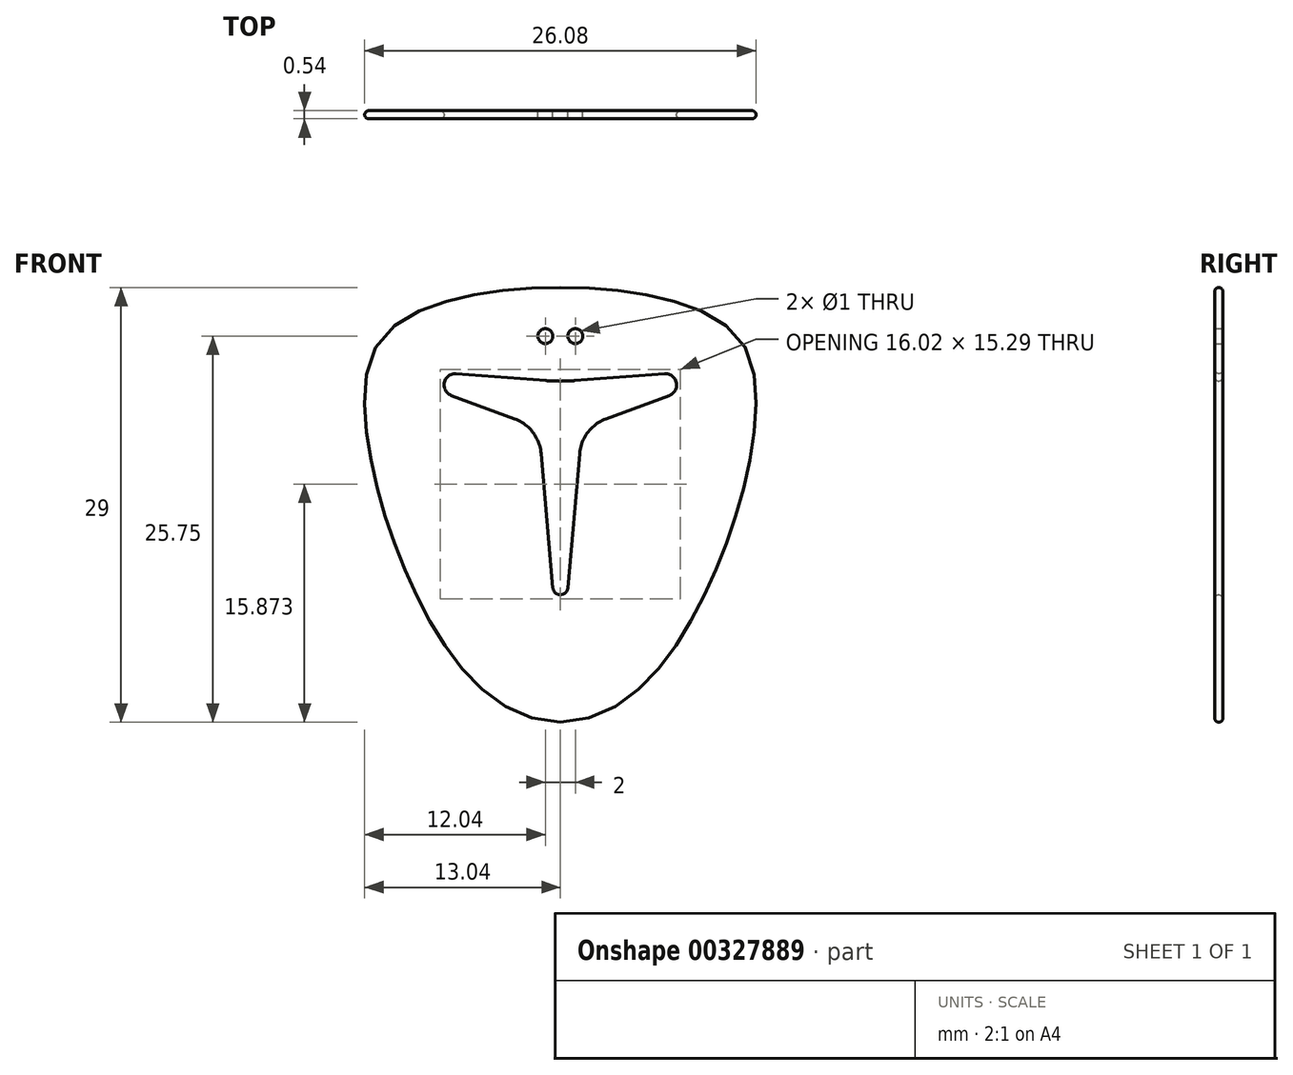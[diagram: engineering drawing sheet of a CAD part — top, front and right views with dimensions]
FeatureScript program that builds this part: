
annotation { "Feature Type Name" : "Feature", "Feature Type Description" : "" }
export const myFeature = defineFeature(function(context is Context, id is Id, definition is map)
    precondition{}
    {
        {
            var Q0;
            Q0=qCreatedBy(makeId("Front.planeOp"),FACE);
            var sketch = newSketch(context, id + "F0", { "sketchPlane" : qUnion([Q0])});
            skLineSegment(sketch, "E0", {"start": v(0, 0) * mm, "end": v(0, 6.5) * mm, "construction": true});
            skLineSegment(sketch, "E1", {"start": v(0, 0) * mm, "end": v(0, -22.5) * mm, "construction": true});
            skLineSegment(sketch, "E2", {"start": v(0, 0) * mm, "end": v(13, 0) * mm, "construction": true});
            skFitSpline(sketch, "E3", {"points": [v(0, -22.5) * mm, v(10.5, -12) * mm, v(13, 0) * mm, v(11, 4) * mm, v(0, 6.5) * mm], "startDerivative": vector(49.93, 0) * mm, "endDerivative": vector(-57.3, 0) * mm});
            skFitSpline(sketch, "E4.MirrorCS", {"points": [v(0, -22.5) * mm, v(-10.5, -12) * mm, v(-13, 0) * mm, v(-11, 4) * mm, v(0, 6.5) * mm], "startDerivative": vector(-49.93, 0) * mm, "endDerivative": vector(57.3, 0) * mm});
            skArc(sketch, "E5", {"start": v(7.26, -0.7) * mm, "mid": v(7.73, 0.16) * mm, "end": v(6.94, 0.75) * mm});
            skLineSegment(sketch, "E6", {"start": v(7.26, -0.7) * mm, "end": v(3.04, -2.27) * mm});
            skArc(sketch, "E7", {"start": v(3.04, -2.27) * mm, "mid": v(1.83, -3.17) * mm, "end": v(1.28, -4.58) * mm});
            skLineSegment(sketch, "E8", {"start": v(0.5, -13.54) * mm, "end": v(1.28, -4.58) * mm});
            skArc(sketch, "E9", {"start": v(0, -14) * mm, "mid": v(0.34, -13.87) * mm, "end": v(0.5, -13.54) * mm});
            skArc(sketch, "E10.MirrorCS", {"start": v(0, -14) * mm, "mid": v(-0.34, -13.87) * mm, "end": v(-0.5, -13.54) * mm});
            skLineSegment(sketch, "E11.MirrorCS", {"start": v(-0.5, -13.54) * mm, "end": v(-1.28, -4.58) * mm});
            skArc(sketch, "E12.MirrorCS", {"start": v(-3.04, -2.27) * mm, "mid": v(-1.83, -3.17) * mm, "end": v(-1.28, -4.58) * mm});
            skLineSegment(sketch, "E13.MirrorCS", {"start": v(-7.26, -0.7) * mm, "end": v(-3.04, -2.27) * mm});
            skArc(sketch, "E14.MirrorCS", {"start": v(-7.26, -0.7) * mm, "mid": v(-7.73, 0.16) * mm, "end": v(-6.94, 0.75) * mm});
            skLineSegment(sketch, "E15", {"start": v(6.94, 0.75) * mm, "end": v(0.96, 0.29) * mm});
            skArc(sketch, "E16", {"start": v(0, 0.25) * mm, "mid": v(0.48, 0.26) * mm, "end": v(0.96, 0.29) * mm});
            skArc(sketch, "E17.MirrorCS", {"start": v(0, 0.25) * mm, "mid": v(-0.48, 0.26) * mm, "end": v(-0.96, 0.29) * mm});
            skLineSegment(sketch, "E18.MirrorCS", {"start": v(-6.94, 0.75) * mm, "end": v(-0.96, 0.29) * mm});
            skLineSegment(sketch, "E19", {"start": v(0, 3.25) * mm, "end": v(1, 3.25) * mm});
            skCircle(sketch, "E20", {"center": v(1, 3.25) * mm, "radius": 0.5 * mm});
            skLineSegment(sketch, "E21.MirrorCS", {"start": v(0, 3.25) * mm, "end": v(-1, 3.25) * mm});
            skCircle(sketch, "E22.MirrorC", {"center": v(-1, 3.25) * mm, "radius": 0.5 * mm});
            skSolve(sketch);
        }
        {
            var Q0;
            Q0=qSketchRegion(id+"F0",true);
            extrude(context, id + "F1", {"entities" : qUnion([Q0]), "depth" : 0.54 * mm});
        }
        {
            var Q0;
            Q0=makeQuery(id+"F1.opExtrude","CAP_EDGE",EDGE,{"disambiguationData":[OSD([sQuery(id+"F0.wireOp",EDGE,"E5")])],"isStart":false});
            var Q1;
            Q1=makeQuery(id+"F1.opExtrude","CAP_EDGE",EDGE,{"disambiguationData":[OSD([sQuery(id+"F0.wireOp",EDGE,"E7")])],"isStart":true});
            var Q2;
            Q2=makeQuery(id+"F1.opExtrude","CAP_EDGE",EDGE,{"disambiguationData":[OSD([sQuery(id+"F0.wireOp",EDGE,"E9"),sQuery(id+"F0.wireOp",EDGE,"E10.MirrorCS")])],"isStart":false});
            var Q3;
            Q3=makeQuery(id+"F1.opExtrude","CAP_EDGE",EDGE,{"disambiguationData":[OSD([sQuery(id+"F0.wireOp",EDGE,"E14.MirrorCS")])],"isStart":false});
            var Q4;
            Q4=makeQuery(id+"F1.opExtrude","CAP_EDGE",EDGE,{"disambiguationData":[OSD([sQuery(id+"F0.wireOp",EDGE,"E5")])],"isStart":true});
            var Q5;
            Q5=makeQuery(id+"F1.opExtrude","CAP_EDGE",EDGE,{"disambiguationData":[OSD([sQuery(id+"F0.wireOp",EDGE,"E12.MirrorCS")])],"isStart":false});
            var Q6;
            Q6=makeQuery(id+"F1.opExtrude","CAP_EDGE",EDGE,{"disambiguationData":[OSD([sQuery(id+"F0.wireOp",EDGE,"E7")])],"isStart":false});
            var Q7;
            Q7=makeQuery(id+"F1.opExtrude","CAP_EDGE",EDGE,{"disambiguationData":[OSD([sQuery(id+"F0.wireOp",EDGE,"cP70XH3B-hxny-nh1n-TbyW-52Zl4TOD4HrO"),sQuery(id+"F0.wireOp",EDGE,"9cf6c757-e815-40dd-95a7-672993b90d513.MirrorCS")])],"isStart":true});
            var Q8;
            Q8=makeQuery(id+"F1.opExtrude","CAP_EDGE",EDGE,{"disambiguationData":[OSD([sQuery(id+"F0.wireOp",EDGE,"E13.MirrorCS")])],"isStart":false});
            var Q9;
            Q9=makeQuery(id+"F1.opExtrude","CAP_EDGE",EDGE,{"disambiguationData":[OSD([sQuery(id+"F0.wireOp",EDGE,"E12.MirrorCS")])],"isStart":true});
            var Q10;
            Q10=makeQuery(id+"F1.opExtrude","CAP_EDGE",EDGE,{"disambiguationData":[OSD([sQuery(id+"F0.wireOp",EDGE,"cP70XH3B-hxny-nh1n-TbyW-52Zl4TOD4HrO"),sQuery(id+"F0.wireOp",EDGE,"9cf6c757-e815-40dd-95a7-672993b90d513.MirrorCS")])],"isStart":false});
            var Q11;
            Q11=makeQuery(id+"F1.opExtrude","CAP_EDGE",EDGE,{"disambiguationData":[OSD([sQuery(id+"F0.wireOp",EDGE,"E9"),sQuery(id+"F0.wireOp",EDGE,"E10.MirrorCS")])],"isStart":true});
            var Q12;
            Q12=makeQuery(id+"F1.opExtrude","SWEPT_EDGE",EDGE,{"disambiguationData":[OSD([sQuery(id+"F0.wireOp",EDGE,"9cf6c757-e815-40dd-95a7-672993b90d513.MirrorCS"),sQuery(id+"F0.wireOp",EDGE,"E14.MirrorCS")])]});
            var Q13;
            Q13=makeQuery(id+"F1.opExtrude","CAP_EDGE",EDGE,{"disambiguationData":[OSD([sQuery(id+"F0.wireOp",EDGE,"E8")])],"isStart":true});
            var Q14;
            Q14=makeQuery(id+"F1.opExtrude","CAP_EDGE",EDGE,{"disambiguationData":[OSD([sQuery(id+"F0.wireOp",EDGE,"E11.MirrorCS")])],"isStart":false});
            var Q15;
            Q15=makeQuery(id+"F1.opExtrude","SWEPT_EDGE",EDGE,{"disambiguationData":[OSD([sQuery(id+"F0.wireOp",EDGE,"E6"),sQuery(id+"F0.wireOp",EDGE,"E7")])]});
            var Q16;
            Q16=makeQuery(id+"F1.opExtrude","SWEPT_EDGE",EDGE,{"disambiguationData":[OSD([sQuery(id+"F0.wireOp",EDGE,"E8"),sQuery(id+"F0.wireOp",EDGE,"E9")])]});
            var Q17;
            Q17=makeQuery(id+"F1.opExtrude","SWEPT_EDGE",EDGE,{"disambiguationData":[OSD([sQuery(id+"F0.wireOp",EDGE,"E13.MirrorCS"),sQuery(id+"F0.wireOp",EDGE,"E14.MirrorCS")])]});
            var Q18;
            Q18=makeQuery(id+"F1.opExtrude","SWEPT_EDGE",EDGE,{"disambiguationData":[OSD([sQuery(id+"F0.wireOp",EDGE,"E10.MirrorCS"),sQuery(id+"F0.wireOp",EDGE,"E11.MirrorCS")])]});
            var Q19;
            Q19=makeQuery(id+"F1.opExtrude","SWEPT_EDGE",EDGE,{"disambiguationData":[OSD([sQuery(id+"F0.wireOp",EDGE,"E11.MirrorCS"),sQuery(id+"F0.wireOp",EDGE,"E12.MirrorCS")])]});
            var Q20;
            Q20=makeQuery(id+"F1.opExtrude","SWEPT_EDGE",EDGE,{"disambiguationData":[OSD([sQuery(id+"F0.wireOp",EDGE,"E5"),sQuery(id+"F0.wireOp",EDGE,"E6")])]});
            var Q21;
            Q21=makeQuery(id+"F1.opExtrude","CAP_EDGE",EDGE,{"disambiguationData":[OSD([sQuery(id+"F0.wireOp",EDGE,"E14.MirrorCS")])],"isStart":true});
            var Q22;
            Q22=makeQuery(id+"F1.opExtrude","SWEPT_EDGE",EDGE,{"disambiguationData":[OSD([sQuery(id+"F0.wireOp",EDGE,"E12.MirrorCS"),sQuery(id+"F0.wireOp",EDGE,"E13.MirrorCS")])]});
            var Q23;
            Q23=makeQuery(id+"F1.opExtrude","CAP_EDGE",EDGE,{"disambiguationData":[OSD([sQuery(id+"F0.wireOp",EDGE,"E8")])],"isStart":false});
            var Q24;
            Q24=makeQuery(id+"F1.opExtrude","SWEPT_EDGE",EDGE,{"disambiguationData":[OSD([sQuery(id+"F0.wireOp",EDGE,"cP70XH3B-hxny-nh1n-TbyW-52Zl4TOD4HrO"),sQuery(id+"F0.wireOp",EDGE,"E5")])]});
            var Q25;
            Q25=makeQuery(id+"F1.opExtrude","CAP_EDGE",EDGE,{"disambiguationData":[OSD([sQuery(id+"F0.wireOp",EDGE,"E6")])],"isStart":false});
            var Q26;
            Q26=makeQuery(id+"F1.opExtrude","CAP_EDGE",EDGE,{"disambiguationData":[OSD([sQuery(id+"F0.wireOp",EDGE,"E11.MirrorCS")])],"isStart":true});
            var Q27;
            Q27=makeQuery(id+"F1.opExtrude","SWEPT_EDGE",EDGE,{"disambiguationData":[OSD([sQuery(id+"F0.wireOp",EDGE,"E7"),sQuery(id+"F0.wireOp",EDGE,"E8")])]});
            var Q28;
            Q28=makeQuery(id+"F1.opExtrude","CAP_EDGE",EDGE,{"disambiguationData":[OSD([sQuery(id+"F0.wireOp",EDGE,"E6")])],"isStart":true});
            var Q29;
            Q29=makeQuery(id+"F1.opExtrude","CAP_EDGE",EDGE,{"disambiguationData":[OSD([sQuery(id+"F0.wireOp",EDGE,"E13.MirrorCS")])],"isStart":true});
            var Q30;
            Q30=makeQuery(id+"F1.opExtrude","CAP_EDGE",EDGE,{"disambiguationData":[OSD([sQuery(id+"F0.wireOp",EDGE,"E18.MirrorCS")])],"isStart":false});
            var Q31;
            Q31=makeQuery(id+"F1.opExtrude","CAP_EDGE",EDGE,{"disambiguationData":[OSD([sQuery(id+"F0.wireOp",EDGE,"E18.MirrorCS")])],"isStart":true});
            var Q32;
            Q32=makeQuery(id+"F1.opExtrude","CAP_EDGE",EDGE,{"disambiguationData":[OSD([sQuery(id+"F0.wireOp",EDGE,"E16"),sQuery(id+"F0.wireOp",EDGE,"E17.MirrorCS")])],"isStart":false});
            var Q33;
            Q33=makeQuery(id+"F1.opExtrude","CAP_EDGE",EDGE,{"disambiguationData":[OSD([sQuery(id+"F0.wireOp",EDGE,"E16"),sQuery(id+"F0.wireOp",EDGE,"E17.MirrorCS")])],"isStart":true});
            var Q34;
            Q34=makeQuery(id+"F1.opExtrude","CAP_EDGE",EDGE,{"disambiguationData":[OSD([sQuery(id+"F0.wireOp",EDGE,"E15")])],"isStart":false});
            fillet(context, id + "F2", {"entities" : qUnion([Q0, Q1, Q2, Q3, Q4, Q5, Q6, Q7, Q8, Q9, Q10, Q11, Q12, Q13, Q14, Q15, Q16, Q17, Q18, Q19, Q20, Q21, Q22, Q23, Q24, Q25, Q26, Q27, Q28, Q29, Q30, Q31, Q32, Q33, Q34]), "radius" : (0.54 / 2) * mm, "tangentPropagation" : true, "allowEdgeOverflow" : false});
        }
        {
            var Q0;
            Q0=makeQuery(id+"F1.opExtrude","CAP_EDGE",EDGE,{"disambiguationData":[OSD([sQuery(id+"F0.wireOp",EDGE,"E4.MirrorCS")])],"isStart":false});
            var Q1;
            Q1=makeQuery(id+"F1.opExtrude","CAP_EDGE",EDGE,{"disambiguationData":[OSD([sQuery(id+"F0.wireOp",EDGE,"E3")])],"isStart":false});
            var Q2;
            Q2=makeQuery(id+"F1.opExtrude","CAP_EDGE",EDGE,{"disambiguationData":[OSD([sQuery(id+"F0.wireOp",EDGE,"E4.MirrorCS")])],"isStart":true});
            var Q3;
            Q3=makeQuery(id+"F1.opExtrude","CAP_EDGE",EDGE,{"disambiguationData":[OSD([sQuery(id+"F0.wireOp",EDGE,"E3")])],"isStart":true});
            fillet(context, id + "F3", {"entities" : qUnion([Q0, Q1, Q2, Q3]), "radius" : 0.54 / 2 * mm, "tangentPropagation" : true, "allowEdgeOverflow" : false});
        }
    });
